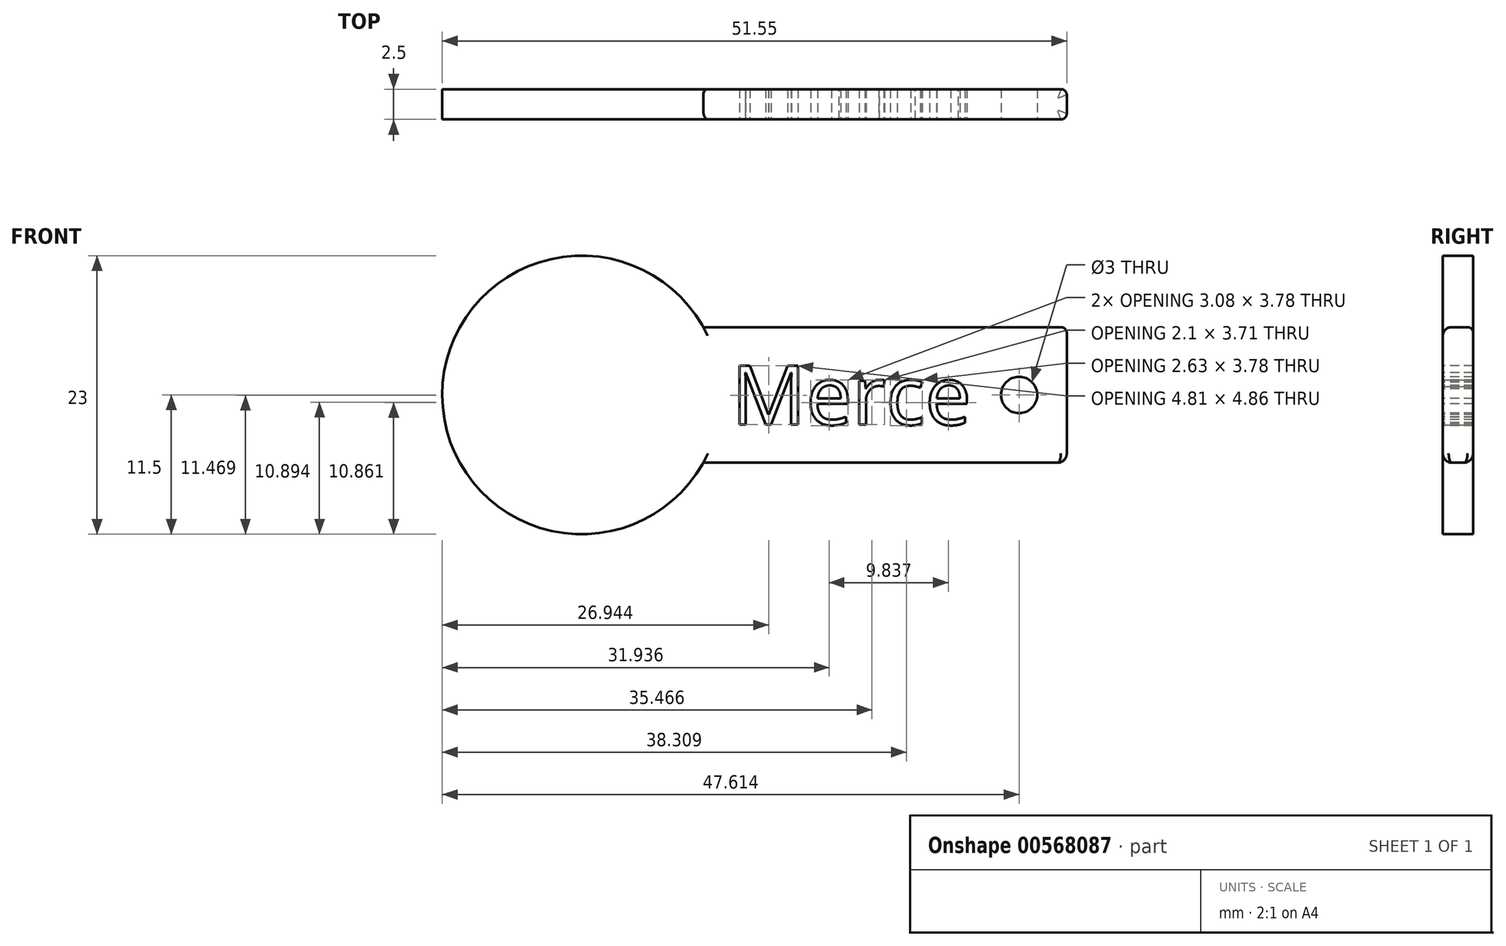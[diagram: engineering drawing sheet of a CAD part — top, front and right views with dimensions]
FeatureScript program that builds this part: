
annotation { "Feature Type Name" : "Feature", "Feature Type Description" : "" }
export const myFeature = defineFeature(function(context is Context, id is Id, definition is map)
    precondition{}
    {
        {
            var Q0;
            Q0=qCreatedBy(makeId("Front.planeOp"),FACE);
            var sketch = newSketch(context, id + "F0", { "sketchPlane" : qUnion([Q0])});
            skCircle(sketch, "E0", {"center": v(-21.17, 0) * mm, "radius": 11.5 * mm});
            skLineSegment(sketch, "E1", {"start": v(-11.12, 5.6) * mm, "end": v(18.88, 5.6) * mm});
            skLineSegment(sketch, "E2", {"start": v(-11.12, -5.6) * mm, "end": v(18.88, -5.6) * mm});
            skLineSegment(sketch, "E3", {"start": v(18.88, 5.6) * mm, "end": v(18.88, -5.6) * mm});
            skSolve(sketch);
        }
        {
            var Q0;
            {var subQ0=sQuery(id+"F0.wireOp",EDGE,"E0");var subQ1=makeQuery(id+"F0.imprint","INTERSECT",VERTEX,{"derivedFrom":[subQ0,sQuery(id+"F0.wireOp",EDGE,"E1")]});Q0=makeQuery(id+"F0.imprint","IMPRINT",FACE,{"disambiguationData":[TD([[makeQuery(id+"F0.imprint","IMPRINT",EDGE,{"disambiguationData":[TD([[subQ1,-1.0]])],"derivedFrom":subQ0}),1.0]])]});}
            var Q1;
            {var subQ0=sQuery(id+"F0.wireOp",EDGE,"E1");Q1=makeQuery(id+"F0.imprint","IMPRINT",FACE,{"disambiguationData":[TD([[makeQuery(id+"F0.imprint","IMPRINT",EDGE,{"derivedFrom":subQ0}),-1.0]])]});}
            extrude(context, id + "F1", {"entities" : qUnion([Q0, Q1]), "depth" : 2.5 * mm, "offsetDistance" : 25 * mm});
        }
        {
            var Q0;
            {var subQ0=sQuery(id+"F0.wireOp",EDGE,"E2");var subQ1=sQuery(id+"F0.wireOp",EDGE,"E0");var subQ2=sQuery(id+"F0.wireOp",EDGE,"E3");var subQ3=sQuery(id+"F0.wireOp",EDGE,"E1");Q0=makeQuery(id+"FJ8alyAhGk8dJ15_1.boolean.opBoolean","SPLIT",FACE,{"disambiguationData":[TD([makeQuery(id+"F1.opExtrude","SWEPT_FACE",FACE,{"disambiguationData":[OSD([subQ1])]})])],"derivedFrom":makeQuery(id+"F1.opExtrude","CAP_FACE",FACE,{"disambiguationData":[OSD([subQ1,subQ3,subQ0,subQ2])],"isStart":false})});}
            var sketch = newSketch(context, id + "F2", { "sketchPlane" : qUnion([Q0])});
            skCircle(sketch, "E4", {"center": v(14.94, 0) * mm, "radius": 1.5 * mm});
            skSolve(sketch);
        }
        {
            var Q0;
            Q0=makeQuery(id+"F2.imprint","IMPRINT",FACE,{"disambiguationData":[TD([[makeQuery(id+"F2.imprint","IMPRINT",EDGE,{"derivedFrom":sQuery(id+"F2.wireOp",EDGE,"E4")}),1.0]])]});
            extrude(context, id + "F3", {"entities" : qUnion([Q0]), "operationType" : NewBodyOperationType.REMOVE, "oppositeDirection" : true, "depth" : 25 * mm, "offsetDistance" : 25 * mm});
        }
        {
            var Q0;
            Q0=makeQuery(id+"F1.opExtrude","CAP_EDGE",EDGE,{"disambiguationData":[OSD([sQuery(id+"F0.wireOp",EDGE,"E1")])],"isStart":false});
            fillet(context, id + "F4", {"entities" : qUnion([Q0]), "radius" : 0.72 * mm, "tangentPropagation" : true, "allowEdgeOverflow" : false});
        }
        {
            var Q0;
            Q0=makeQuery(id+"F1.opExtrude","CAP_EDGE",EDGE,{"disambiguationData":[OSD([sQuery(id+"F0.wireOp",EDGE,"E3")])],"isStart":false});
            fillet(context, id + "F5", {"entities" : qUnion([Q0]), "radius" : 0.48 * mm, "tangentPropagation" : true, "allowEdgeOverflow" : false});
        }
        {
            var Q0;
            Q0=makeQuery(id+"F1.opExtrude","CAP_EDGE",EDGE,{"disambiguationData":[OSD([sQuery(id+"F0.wireOp",EDGE,"E3")])],"isStart":true});
            fillet(context, id + "F6", {"entities" : qUnion([Q0]), "radius" : 0.46 * mm, "tangentPropagation" : true, "allowEdgeOverflow" : false});
        }
        {
            var Q0;
            Q0=makeQuery(id+"F1.opExtrude","CAP_EDGE",EDGE,{"disambiguationData":[OSD([sQuery(id+"F0.wireOp",EDGE,"E2")])],"isStart":false});
            fillet(context, id + "F7", {"entities" : qUnion([Q0]), "radius" : 0.77 * mm, "tangentPropagation" : true, "allowEdgeOverflow" : false});
        }
        {
            var Q0;
            Q0=makeQuery(id+"F1.opExtrude","CAP_FACE",FACE,{"disambiguationData":[OSD([sQuery(id+"F0.wireOp",EDGE,"E0"),sQuery(id+"F0.wireOp",EDGE,"E1"),sQuery(id+"F0.wireOp",EDGE,"E2"),sQuery(id+"F0.wireOp",EDGE,"E3")])],"isStart":false});
            var sketch = newSketch(context, id + "F8", { "sketchPlane" : qUnion([Q0])});
            skText(sketch, "E5", { "text": "Merce\n", "fontName": "OpenSans-Regular.ttf"});
            const initialGuessF8  = {"E5": [-0.0088, -0.00246, 1, 0, 0.0049]};
            skSetInitialGuess(sketch, initialGuessF8);
            skSolve(sketch);
        }
        {
            var Q0;
            Q0=makeQuery(id+"F8.imprint","IMPRINT",FACE,{"disambiguationData":[TD([[makeQuery(id+"F8.imprint","IMPRINT",EDGE,{"derivedFrom":sQuery(id+"F8.wireOp",EDGE,"E5.sketch_text.stroke-0")}),-1.0]])]});
            var Q1;
            Q1=makeQuery(id+"F8.imprint","IMPRINT",FACE,{"disambiguationData":[TD([[makeQuery(id+"F8.imprint","IMPRINT",EDGE,{"derivedFrom":sQuery(id+"F8.wireOp",EDGE,"E5.sketch_text.stroke-18")}),-1.0]])]});
            var Q2;
            Q2=makeQuery(id+"F8.imprint","IMPRINT",FACE,{"disambiguationData":[TD([[makeQuery(id+"F8.imprint","IMPRINT",EDGE,{"derivedFrom":sQuery(id+"F8.wireOp",EDGE,"E5.sketch_text.stroke-37")}),-1.0]])]});
            var Q3;
            Q3=makeQuery(id+"F8.imprint","IMPRINT",FACE,{"disambiguationData":[TD([[makeQuery(id+"F8.imprint","IMPRINT",EDGE,{"derivedFrom":sQuery(id+"F8.wireOp",EDGE,"E5.sketch_text.stroke-50")}),-1.0]])]});
            var Q4;
            Q4=makeQuery(id+"F8.imprint","IMPRINT",FACE,{"disambiguationData":[TD([[makeQuery(id+"F8.imprint","IMPRINT",EDGE,{"derivedFrom":sQuery(id+"F8.wireOp",EDGE,"E5.sketch_text.stroke-65")}),-1.0]])]});
            extrude(context, id + "F9", {"entities" : qUnion([Q0, Q1, Q2, Q3, Q4]), "operationType" : NewBodyOperationType.REMOVE, "oppositeDirection" : true, "depth" : 25 * mm, "offsetDistance" : 25 * mm});
        }
    });
